# Revit family: Fiber optic splicing cassette for HD modular panel
name_source: partatom
category: Installations électriques
units: mm (PartAtom-declared; Revit-internal decimal feet)

## family parameters
Conserver l'orientation des annotations = Non
Cote de connecteur circulaire = Utiliser le diamètre
Couper avec des vides une fois chargée = Non
Hôte = Face
Partagée = Oui
Point de calcul de pièce = Non
Type d'élément = Normal

## types (1)
- Fiber optic splicing cassette for HD modular panel
    Application class = EC000762
    BIM wording = Legrand FIBER PATCH PANELS
    Description = Fiber optic splicing cassette for HD modular panel
    E-catalogue link = https://www.legrand.fr
    Elévation par défaut = 1219 mm
    Fabricant = LEGRAND
    Function = Fiber optic splicing cassette
    GTIN = 3414970962126
    General Conditions of Use = https://export.legrand.com
    Height (mm) = 44 mm
    Legrand part number = LG-032141
    Length = 185 mm  [stored 0.606955 ft]
    Width (mm) = 110 mm

note: [stored X ft] marks values corroborated as IEEE doubles in the binary element streams (Revit-internal decimal feet)
